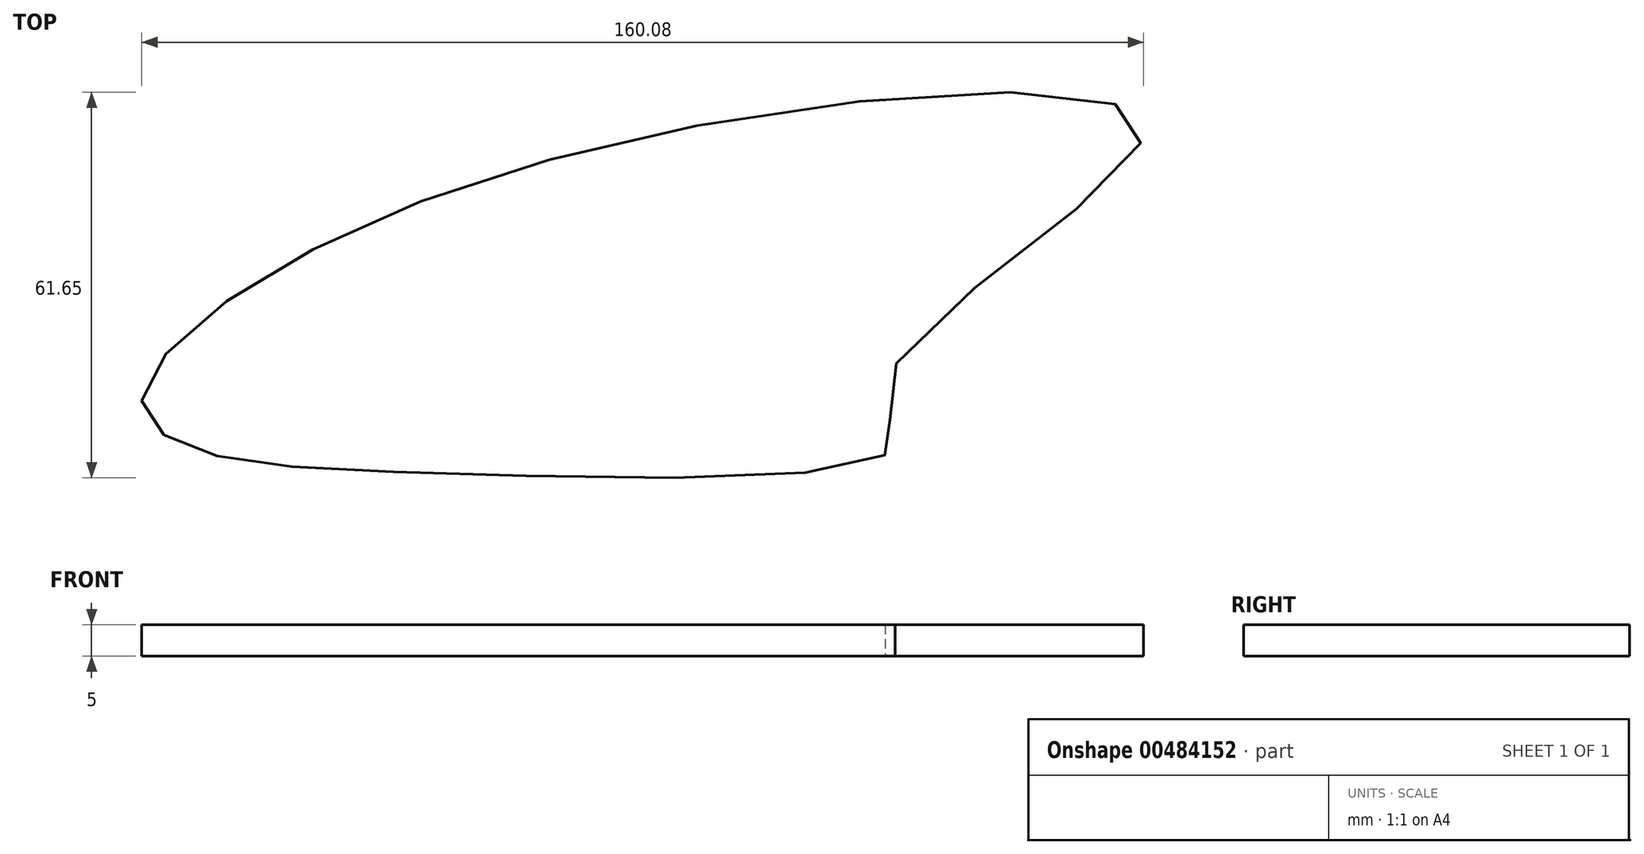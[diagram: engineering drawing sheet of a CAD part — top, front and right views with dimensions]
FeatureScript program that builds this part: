
annotation { "Feature Type Name" : "Feature", "Feature Type Description" : "" }
export const myFeature = defineFeature(function(context is Context, id is Id, definition is map)
    precondition{}
    {
        {
            var Q0;
            Q0=qCreatedBy(makeId("Top.planeOp"),FACE);
            var sketch = newSketch(context, id + "F0", { "sketchPlane" : qUnion([Q0])});
            skFitSpline(sketch, "E0", {"points": [v(-75.19, 24.22) * mm, v(2.96, 52.84) * mm, v(71.24, 50.74) * mm, v(30.48, 11.75) * mm, v(31.24, 0.74) * mm, v(-39.23, -3.4) * mm, v(-81.06, 0.74) * mm, v(-88.76, 7.7) * mm, v(-75.19, 24.22) * mm]});
            skLineSegment(sketch, "E1", {"start": v(-88.76, 7.7) * mm, "end": v(43.47, 7.7) * mm, "construction": true});
            skSolve(sketch);
        }
        {
            var Q0;
            Q0=makeQuery(id+"F0.imprint","IMPRINT",FACE,{"disambiguationData":[TD([[makeQuery(id+"F0.imprint","IMPRINT",EDGE,{"derivedFrom":sQuery(id+"F0.wireOp",EDGE,"E0")}),-1.0]])]});
            extrude(context, id + "F1", {"entities" : qUnion([Q0]), "depth" : 5 * mm, "offsetDistance" : 25 * mm});
        }
    });
